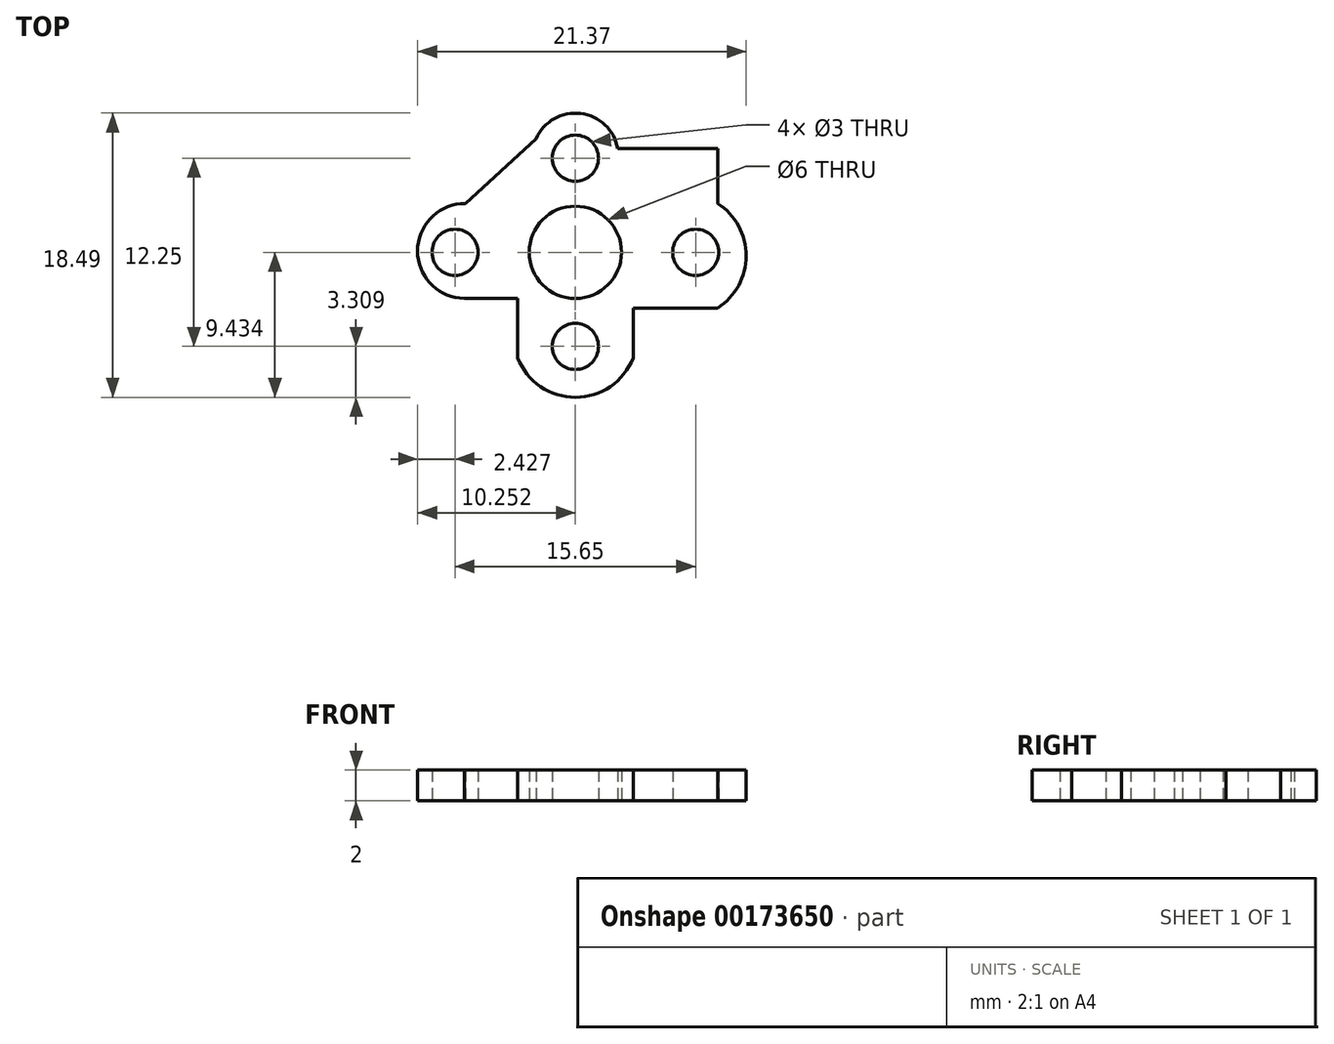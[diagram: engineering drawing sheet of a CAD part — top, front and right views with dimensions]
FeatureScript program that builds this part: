
annotation { "Feature Type Name" : "Feature", "Feature Type Description" : "" }
export const myFeature = defineFeature(function(context is Context, id is Id, definition is map)
    precondition{}
    {
        {
            var Q0;
            Q0=qCreatedBy(makeId("Top.planeOp"),FACE);
            var sketch = newSketch(context, id + "F0", { "sketchPlane" : qUnion([Q0])});
            skLineSegment(sketch, "E0", {"start": v(-24.74, 27.42) * mm, "end": v(-24.74, 1.92) * mm, "construction": true});
            skLineSegment(sketch, "E1", {"start": v(-39.99, 14.67) * mm, "end": v(-9.49, 14.67) * mm, "construction": true});
            skCircle(sketch, "E2", {"center": v(-24.74, 14.67) * mm, "radius": 3 * mm});
            skLineSegment(sketch, "E3.left", {"start": v(-9.49, 27.42) * mm, "end": v(-9.49, 23.67) * mm, "construction": true});
            skCircle(sketch, "E4", {"center": v(-24.74, 14.67) * mm, "radius": 7.83 * mm, "construction": true});
            skCircle(sketch, "E5", {"center": v(-32.56, 14.67) * mm, "radius": 1.5 * mm});
            skCircle(sketch, "E6", {"center": v(-16.91, 14.67) * mm, "radius": 1.5 * mm});
            skCircle(sketch, "E7", {"center": v(-24.74, 14.67) * mm, "radius": 6.12 * mm, "construction": true});
            skCircle(sketch, "E8", {"center": v(-24.74, 20.8) * mm, "radius": 1.5 * mm});
            skCircle(sketch, "E9", {"center": v(-24.74, 8.55) * mm, "radius": 1.5 * mm});
            skLineSegment(sketch, "E10", {"start": v(-9.49, 27.42) * mm, "end": v(-15.49, 27.42) * mm});
            skCircle(sketch, "E11", {"center": v(-18.61, 14.67) * mm, "radius": 1.5 * mm, "construction": true});
            skCircle(sketch, "E12", {"center": v(-30.86, 14.67) * mm, "radius": 1.5 * mm, "construction": true});
            skLineSegment(sketch, "E13.top", {"start": v(-28.49, 11.67) * mm, "end": v(-31.96, 11.67) * mm});
            skLineSegment(sketch, "E13.left", {"start": v(-28.49, 7.8) * mm, "end": v(-28.49, 11.67) * mm});
            skLineSegment(sketch, "E14", {"start": v(-15.49, 21.42) * mm, "end": v(-21.99, 21.42) * mm});
            skLineSegment(sketch, "E15", {"start": v(-34.99, 14.48) * mm, "end": v(-34.99, 15.04) * mm});
            skLineSegment(sketch, "E16", {"start": v(-21.99, 22) * mm, "end": v(-21.99, 21.42) * mm});
            skLineSegment(sketch, "E17", {"start": v(-15.49, 21.42) * mm, "end": v(-15.49, 17.85) * mm});
            skLineSegment(sketch, "E18", {"start": v(-15.49, 11.05) * mm, "end": v(-20.98, 11.05) * mm});
            skLineSegment(sketch, "E19", {"start": v(-20.98, 11.05) * mm, "end": v(-20.98, 7.8) * mm});
            skArc(sketch, "E20", {"start": v(-28.49, 7.8) * mm, "mid": v(-24.73, 5.24) * mm, "end": v(-20.98, 7.8) * mm});
            skArc(sketch, "E21", {"start": v(-15.49, 11.05) * mm, "mid": v(-13.62, 14.45) * mm, "end": v(-15.49, 17.85) * mm});
            skLineSegment(sketch, "E22", {"start": v(-15.49, 17.85) * mm, "end": v(-36.3, 17.85) * mm, "construction": true});
            skArc(sketch, "E23", {"start": v(-31.89, 17.85) * mm, "mid": v(-35, 14.8) * mm, "end": v(-31.96, 11.67) * mm});
            skArc(sketch, "E24", {"start": v(-21.99, 21.42) * mm, "mid": v(-24.4, 23.7) * mm, "end": v(-27.29, 22.07) * mm});
            skPoint(sketch, "E25.MirrorCS.end.orphan", {"position": v(-24.74, 23.73) * mm});
            skPoint(sketch, "E25.MirrorCS.start.orphan", {"position": v(-27.49, 23.73) * mm});
            skPoint(sketch, "E26.orphan", {"position": v(-21.99, 23.73) * mm});
            skLineSegment(sketch, "E27", {"start": v(-31.89, 17.85) * mm, "end": v(-27.29, 22.07) * mm});
            skSolve(sketch);
        }
        {
            var Q0;
            Q0=makeQuery(id+"F0.imprint","IMPRINT",FACE,{"disambiguationData":[TD([[makeQuery(id+"F0.imprint","IMPRINT",EDGE,{"derivedFrom":sQuery(id+"F0.wireOp",EDGE,"E2")}),-1.0]])]});
            extrude(context, id + "F1", {"entities" : qUnion([Q0]), "depth" : 2 * mm});
        }
    });
